# Revit family: PRD_FrankeWS_ShwrFttngsPckg_ShowerPipe_ACSX2001_ACSX2002_ACXX2003_V1
name_source: partatom
category: Specialty Equipment
revit_build: Autodesk Revit 2018 (Build: 20190510_1515(x64)
units: mm (PartAtom-declared; Revit-internal decimal feet)

## family parameters
Always vertical = Yes
Cut with Voids When Loaded = No
OmniClass Number = 23.45.05.14.99
OmniClass Title = Other Sanitary Washing Plumbing Fixtures
Part Type = Normal
Room Calculation Point = No
Round Connector Dimension = Use Diameter
Shared = No
Work Plane-Based = No

## types (3) — shared parameters
AssetType = Fixed
BodyMaterial = PRD_AR_ChromatedBrass_HighPolished
Category = Pr_40_20_87_75, Shower fittings package
Color = Chrome
DurationUnit = year
Finish = Polished chrome
IfcExportAs = IfcPipeFittingType
IfcExportType = USERDEFINED
Manufacturer = KWC Group AG
ManufacturerName = KWC Group AG
ManufacturerURL = www.kwc.com
Material = Brass
NBSDescription = Shower fittings package
NBSReference = 45-35-70/330
NominalHeight = 1200 mm
PressureClass = 0.0 Pa
PressureRange = 0.0 Pa
ProductInformation = https://pim.kwc.com
Status = New
TemperatureRange = 0 °C
TypeOfShowerPipe = Shower pipe
URL = www.kwc.com
Uniclass2015Code = Pr_40_20_87_75
Uniclass2015Title = Shower fittings package
Version = 1
WarrantyDurationUnit = year
WithCrank = Yes
zero-valued in all types: FittingLossFactor, NominalDepth, NominalWidth

## per-type parameters (varying)
| type | BIMObjectName | Crank | CrankOffset | Description | Features | GrossWeight | IntegralAccessories | ModelNumber | Name | NetWeight | ProductCode | Uniclass2015Version |
| ACSX2002 | PRD_AR_ShowerFittingsPackage_ShowerPipe_ACSX2002 | 75.00 mm | 75 mm | Shower pipe for surface installation for connection to F5S self-closing showers, polished chromium-plated brass, with union nut. | Diameter 18 x 0.8 mm, length 1200 mm, crank 75 mm | 0.54 kg |  | 2030041522 | Shower pipe ACSX2002 | 0.50 kg | 210.0636.673 | Products v1.17 |
| ACSX2001 | PRD_AR_ShowerFittingsPackage_ShowerPipe_ACSX2001 | 39.00 mm | 39 mm  [stored 0.127953 ft] | Shower pipe for surface installation for connection to F3S self-closing showers, polished chromium-plated brass, with union nut. Diameter 18 x 0.8 mm, length 1200 mm, crank 39 mm. | Diameter 18 x 0.8 mm, length 1200 mm, crank 39 mm | 0.60 kg | with union nut | 2030039555 | F3 Shower pipe ACSX2001 | 0.55 kg | 210.0597.542 | Products v1.23 |
| ACXX2003 | PRD_AR_ShowerFittingsPackage_ShowerPipe_ACXX2003 | 96.00 mm | 96 mm  [stored 0.314961 ft] | Shower pipe for surface installation for connection to F5E-Therm electronic showers and F5L lever mixer, polished chromium-plated brass, with union nut. Diameter 18 x 0.8 mm, length 1200 mm, crank 96 mm. | Diameter 18 x 0.8 mm, length 1200 mm, crank 96 mm | 0.52 kg | with union nut | 2030041525 | F5 Shower pipe ACXX2003 | 0.50 kg |  | Products v1.23 |

note: column(s) folded — value = type name in every type: Model, ModelReference

note: [stored X ft] marks values corroborated as IEEE doubles in the binary element streams (Revit-internal decimal feet)

## geometry (parser evidence)
native form markers: Sweep x2
no freeform markers — native parametric forms only
